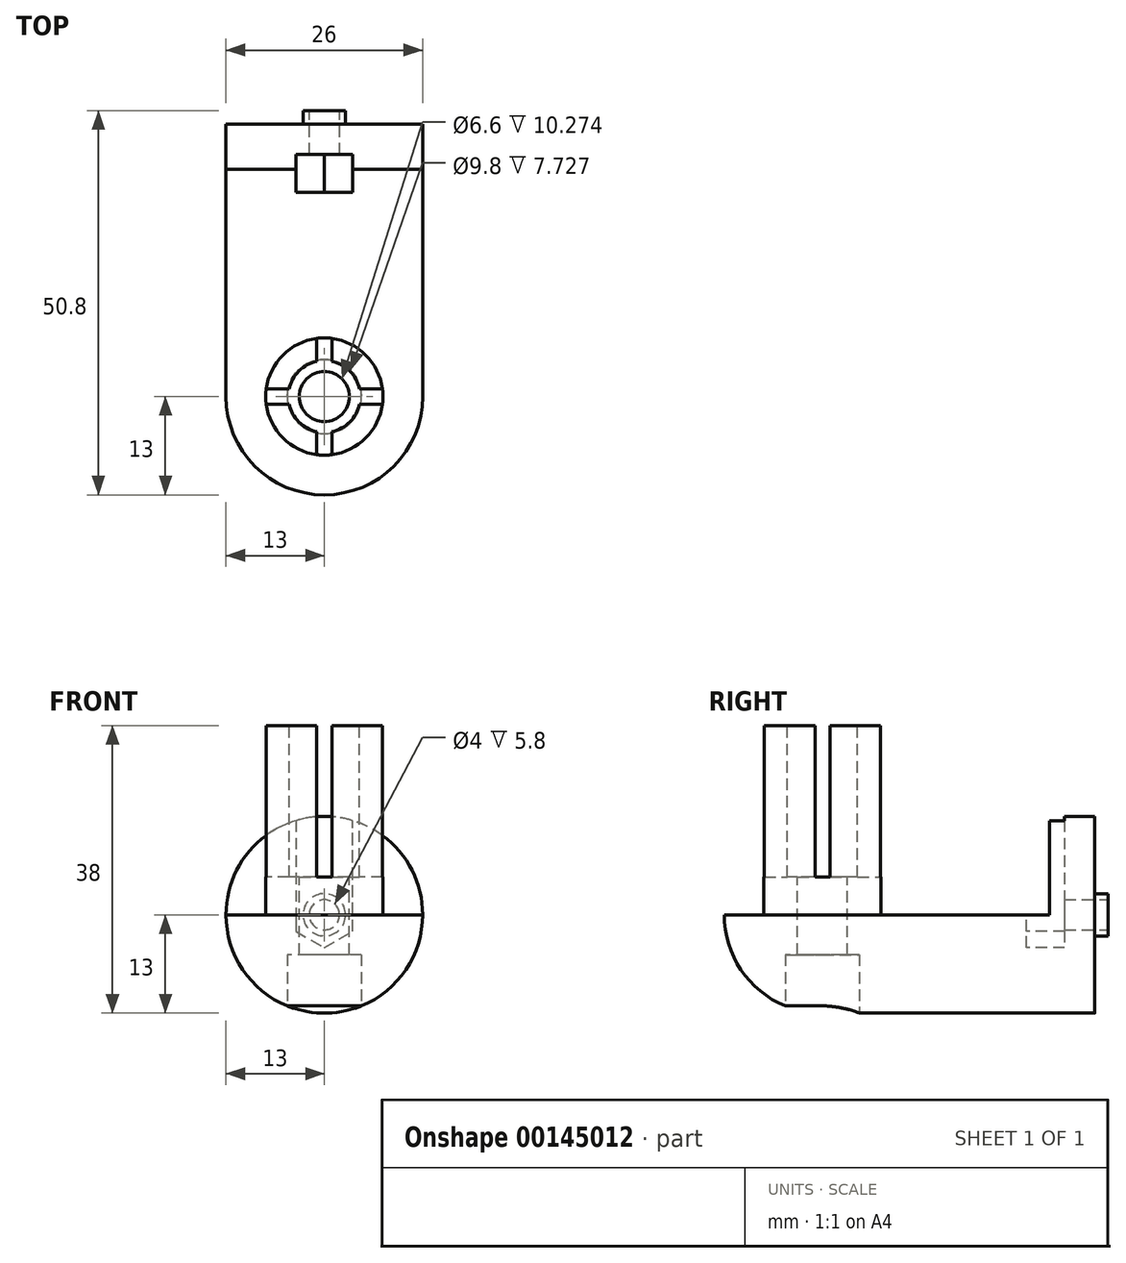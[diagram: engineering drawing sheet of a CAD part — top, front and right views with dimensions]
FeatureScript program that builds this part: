
annotation { "Feature Type Name" : "Feature", "Feature Type Description" : "" }
export const myFeature = defineFeature(function(context is Context, id is Id, definition is map)
    precondition{}
    {
        {
            var Q0;
            Q0=qCreatedBy(makeId("Top.planeOp"),FACE);
            var sketch = newSketch(context, id + "F0", { "sketchPlane" : qUnion([Q0])});
            skLineSegment(sketch, "E0", {"start": v(0, 0) * mm, "end": v(13, 0) * mm});
            skLineSegment(sketch, "E1", {"start": v(13, 0) * mm, "end": v(13, -30) * mm});
            skLineSegment(sketch, "E2", {"start": v(0, -43) * mm, "end": v(0, -43) * mm});
            skLineSegment(sketch, "E3", {"start": v(0, -43) * mm, "end": v(0, 0) * mm});
            skPoint(sketch, "E4.visualSharp", {"position": v(13, -43) * mm});
            skArc(sketch, "E4.filletArc", {"start": v(0, -43) * mm, "mid": v(9.2, -39.2) * mm, "end": v(13, -30) * mm});
            skSolve(sketch);
        }
        {
            var Q0;
            Q0 = qSketchRegion(id + "F0", true);
            var Q1;
            Q1=sQuery(id+"F0.wireOp",EDGE,"E3");
            revolve(context, id + "F1", {"entities" : qUnion([Q0]), "axis" : qUnion([Q1]), "revolveType" : RevolveType.ONE_DIRECTION, "angle" : 180 * degree});
        }
        {
            var Q0;
            Q0=makeQuery(id+"F1.opRevolve","SWEPT_FACE",FACE,{"disambiguationData":[OSD([sQuery(id+"F0.wireOp",EDGE,"E0")])]});
            var sketch = newSketch(context, id + "F2", { "sketchPlane" : qUnion([Q0])});
            skCircle(sketch, "E5", {"center": v(0, 0) * mm, "radius": 13 * mm});
            skSolve(sketch);
        }
        {
            var Q0;
            Q0 = qSketchRegion(id + "F2", true);
            extrude(context, id + "F3", {"entities" : qUnion([Q0]), "operationType" : NewBodyOperationType.ADD, "depth" : 6 * mm});
        }
        {
            var Q0;
            Q0=makeQuery(id+"F3.opExtrude","CAP_FACE",FACE,{"disambiguationData":[OSD([sQuery(id+"F2.wireOp",EDGE,"E5")])],"isStart":false});
            var sketch = newSketch(context, id + "F4", { "sketchPlane" : qUnion([Q0])});
            skCircle(sketch, "E6", {"center": v(0, 0) * mm, "radius": 2 * mm});
            skSolve(sketch);
        }
        {
            var Q0;
            Q0 = qSketchRegion(id + "F4", true);
            extrude(context, id + "F5", {"entities" : qUnion([Q0]), "operationType" : NewBodyOperationType.REMOVE, "oppositeDirection" : true, "depth" : 6 * mm});
        }
        {
            var Q0;
            Q0=makeQuery(id+"F5.boolean.opBoolean","COPY",FACE,{"derivedFrom":makeQuery(id+"F5.opExtrude","CAP_FACE",FACE,{"disambiguationData":[OSD([sQuery(id+"F4.wireOp",EDGE,"E6")])],"isStart":false})});
            var sketch = newSketch(context, id + "F6", { "sketchPlane" : qUnion([Q0])});
            skCircle(sketch, "E7.cCircle", {"center": v(0, 0) * mm, "radius": 3.75 * mm, "construction": true});
            skLineSegment(sketch, "E7.0", {"start": v(0, 4.33) * mm, "end": v(3.75, 2.17) * mm});
            skLineSegment(sketch, "E7.1", {"start": v(3.75, 2.17) * mm, "end": v(3.75, -2.17) * mm});
            skLineSegment(sketch, "E7.2", {"start": v(3.75, -2.17) * mm, "end": v(0, -4.33) * mm});
            skLineSegment(sketch, "E7.3", {"start": v(0, -4.33) * mm, "end": v(-3.75, -2.17) * mm});
            skLineSegment(sketch, "E7.4", {"start": v(-3.75, -2.17) * mm, "end": v(-3.75, 2.17) * mm});
            skLineSegment(sketch, "E7.5", {"start": v(-3.75, 2.17) * mm, "end": v(0, 4.33) * mm});
            skPoint(sketch, "E7.0.midPoint", {"position": v(1.88, 3.25) * mm});
            skSolve(sketch);
        }
        {
            var Q0;
            Q0 = qSketchRegion(id + "F6", true);
            extrude(context, id + "F7", {"entities" : qUnion([Q0]), "operationType" : NewBodyOperationType.REMOVE, "depth" : 2 * mm});
        }
        {
            var Q0;
            Q0=makeQuery(id+"F7.boolean.opBoolean","COPY",FACE,{"derivedFrom":makeQuery(id+"F7.opExtrude","CAP_FACE",FACE,{"disambiguationData":[OSD([sQuery(id+"F6.wireOp",EDGE,"E7.0"),sQuery(id+"F6.wireOp",EDGE,"E7.1"),sQuery(id+"F6.wireOp",EDGE,"E7.2"),sQuery(id+"F6.wireOp",EDGE,"E7.3"),sQuery(id+"F6.wireOp",EDGE,"E7.4"),sQuery(id+"F6.wireOp",EDGE,"E7.5")])],"isStart":false})});
            extrude(context, id + "F8", {"entities" : qUnion([Q0]), "operationType" : NewBodyOperationType.REMOVE, "depth" : 5 * mm});
        }
        {
            var Q0;
            Q0=makeQuery(id+"F7.boolean.opBoolean","MERGE",FACE,{"derivedFrom":[makeQuery(id+"F5.boolean.opBoolean","COPY",FACE,{"derivedFrom":makeQuery(id+"F5.opExtrude","CAP_FACE",FACE,{"disambiguationData":[OSD([sQuery(id+"F4.wireOp",EDGE,"E6")])],"isStart":false})}),makeQuery(id+"F7.opExtrude","CAP_FACE",FACE,{"disambiguationData":[OSD([sQuery(id+"F6.wireOp",EDGE,"E7.0"),sQuery(id+"F6.wireOp",EDGE,"E7.1"),sQuery(id+"F6.wireOp",EDGE,"E7.2"),sQuery(id+"F6.wireOp",EDGE,"E7.3"),sQuery(id+"F6.wireOp",EDGE,"E7.4"),sQuery(id+"F6.wireOp",EDGE,"E7.5")])],"isStart":true})]});
            extrude(context, id + "F9", {"entities" : qUnion([Q0]), "operationType" : NewBodyOperationType.REMOVE, "oppositeDirection" : true, "depth" : 3 * mm});
        }
        {
            var Q0;
            Q0=makeQuery(id+"F3.opExtrude","CAP_FACE",FACE,{"disambiguationData":[OSD([sQuery(id+"F2.wireOp",EDGE,"E5")])],"isStart":true});
            var sketch = newSketch(context, id + "F10", { "sketchPlane" : qUnion([Q0])});
            skLineSegment(sketch, "E8", {"start": v(3.75, 2.17) * mm, "end": v(-3.75, 2.17) * mm});
            skLineSegment(sketch, "E9", {"start": v(-3.75, 2.17) * mm, "end": v(-3.75, 14.3) * mm});
            skLineSegment(sketch, "E10", {"start": v(-3.75, 14.3) * mm, "end": v(3.75, 14.3) * mm});
            skLineSegment(sketch, "E11", {"start": v(3.75, 14.3) * mm, "end": v(3.75, 2.17) * mm});
            skSolve(sketch);
        }
        {
            var Q0;
            Q0 = qSketchRegion(id + "F10", true);
            extrude(context, id + "F11", {"entities" : qUnion([Q0]), "operationType" : NewBodyOperationType.REMOVE, "oppositeDirection" : true, "depth" : 2 * mm});
        }
        {
            var Q0;
            Q0=makeQuery(id+"F3.opExtrude","CAP_FACE",FACE,{"disambiguationData":[OSD([sQuery(id+"F2.wireOp",EDGE,"E5")])],"isStart":false});
            var sketch = newSketch(context, id + "F12", { "sketchPlane" : qUnion([Q0])});
            skCircle(sketch, "E12", {"center": v(0, 0) * mm, "radius": 2.8 * mm});
            skSolve(sketch);
        }
        {
            var Q0;
            Q0=makeQuery(id+"F12.imprint","IMPRINT",FACE,{"disambiguationData":[TD([[makeQuery(id+"F12.imprint","IMPRINT",EDGE,{"derivedFrom":sQuery(id+"F12.wireOp",EDGE,"E12")}),1.0]])]});
            extrude(context, id + "F13", {"entities" : qUnion([Q0]), "operationType" : NewBodyOperationType.ADD, "depth" : 1.8 * mm});
        }
        {
            var Q0;
            Q0=makeQuery(id+"F1.opRevolve","CAP_FACE",FACE,{"disambiguationData":[OSD([sQuery(id+"F0.wireOp",EDGE,"E0"),sQuery(id+"F0.wireOp",EDGE,"E1"),sQuery(id+"F0.wireOp",EDGE,"E3"),sQuery(id+"F0.wireOp",EDGE,"E4.filletArc")])],"isStart":false});
            var sketch = newSketch(context, id + "F14", { "sketchPlane" : qUnion([Q0])});
            skCircle(sketch, "E13", {"center": v(0, -30) * mm, "radius": 3.3 * mm});
            skSolve(sketch);
        }
        {
            var Q0;
            Q0 = qSketchRegion(id + "F14", true);
            extrude(context, id + "F15", {"entities" : qUnion([Q0]), "operationType" : NewBodyOperationType.REMOVE, "oppositeDirection" : true, "depth" : 25 * mm});
        }
        {
            var Q0;
            Q0=makeQuery(id+"F15.boolean.opBoolean","INTERSECT",EDGE,{"derivedFrom":[makeQuery(id+"F1.opRevolve","SWEPT_FACE",FACE,{"disambiguationData":[OSD([sQuery(id+"F0.wireOp",EDGE,"E4.filletArc")])]}),makeQuery(id+"F15.opExtrude","SWEPT_FACE",FACE,{"disambiguationData":[OSD([sQuery(id+"F14.wireOp",EDGE,"E13")])]})]});
            var Q1;
            Q1=makeQuery(id+"F15.boolean.opBoolean","INTERSECT",VERTEX,{"disambiguationData":[OD(1.0)],"derivedFrom":[makeQuery(id+"F1.opRevolve","SWEPT_FACE",FACE,{"disambiguationData":[OSD([sQuery(id+"F0.wireOp",EDGE,"E4.filletArc")])]}),makeQuery(id+"F3.boolean.opBoolean","MERGE",FACE,{"derivedFrom":[makeQuery(id+"F1.opRevolve","SWEPT_FACE",FACE,{"disambiguationData":[OSD([sQuery(id+"F0.wireOp",EDGE,"E1")])]}),makeQuery(id+"F3.opExtrude","SWEPT_FACE",FACE,{"disambiguationData":[OSD([sQuery(id+"F2.wireOp",EDGE,"E5")])]})]}),makeQuery(id+"F15.opExtrude","SWEPT_FACE",FACE,{"disambiguationData":[OSD([sQuery(id+"F14.wireOp",EDGE,"E13")])]})]});
            cPlane(context, id + "F16", {"entities" : qUnion([Q0, Q1]), "cplaneType" : CPlaneType.LINE_POINT, "offset" : 25 * mm, "width" : 150 * mm, "height" : 150 * mm});
        }
        {
            var Q0;
            Q0=qCreatedBy(id+"F16.planeOp",FACE);
            var sketch = newSketch(context, id + "F17", { "sketchPlane" : qUnion([Q0])});
            skCircle(sketch, "E14", {"center": v(0, -30) * mm, "radius": 4.9 * mm});
            skSolve(sketch);
        }
        {
            var Q0;
            Q0 = qSketchRegion(id + "F17", true);
            extrude(context, id + "F18", {"entities" : qUnion([Q0]), "operationType" : NewBodyOperationType.REMOVE, "depth" : 7.3 * mm});
        }
        {
            var Q0;
            Q0=makeQuery(id+"F18.boolean.opBoolean","COPY",FACE,{"derivedFrom":makeQuery(id+"F18.opExtrude","CAP_FACE",FACE,{"disambiguationData":[OSD([sQuery(id+"F17.wireOp",EDGE,"E14")])],"isStart":false})});
            extrude(context, id + "F19", {"entities" : qUnion([Q0]), "operationType" : NewBodyOperationType.REMOVE, "depth" : 25 * mm});
        }
        {
            var Q0;
            Q0=makeQuery(id+"F1.opRevolve","CAP_FACE",FACE,{"disambiguationData":[OSD([sQuery(id+"F0.wireOp",EDGE,"E0"),sQuery(id+"F0.wireOp",EDGE,"E1"),sQuery(id+"F0.wireOp",EDGE,"E3"),sQuery(id+"F0.wireOp",EDGE,"E4.filletArc")])],"isStart":false});
            var sketch = newSketch(context, id + "F20", { "sketchPlane" : qUnion([Q0])});
            skCircle(sketch, "E15", {"center": v(0, -30) * mm, "radius": 7.75 * mm});
            skSolve(sketch);
        }
        {
            var Q0;
            Q0=makeQuery(id+"F20.imprint","IMPRINT",FACE,{"disambiguationData":[TD([[makeQuery(id+"F20.imprint","IMPRINT",EDGE,{"derivedFrom":sQuery(id+"F20.wireOp",EDGE,"E15")}),1.0]])]});
            extrude(context, id + "F21", {"entities" : qUnion([Q0]), "operationType" : NewBodyOperationType.ADD, "depth" : 25 * mm});
        }
        {
            var Q0;
            Q0=makeQuery(id+"F21.opExtrude","CAP_FACE",FACE,{"disambiguationData":[OSD([sQuery(id+"F14.wireOp",EDGE,"E13"),sQuery(id+"F20.wireOp",EDGE,"E15")])],"isStart":false});
            var sketch = newSketch(context, id + "F22", { "sketchPlane" : qUnion([Q0])});
            skCircle(sketch, "E16", {"center": v(0, -30) * mm, "radius": 4.75 * mm});
            skLineSegment(sketch, "E17.bottom", {"start": v(1, -40.1) * mm, "end": v(-1, -40.1) * mm});
            skLineSegment(sketch, "E17.top", {"start": v(1, -19.9) * mm, "end": v(-1, -19.9) * mm});
            skLineSegment(sketch, "E17.left", {"start": v(1, -40.1) * mm, "end": v(1, -19.9) * mm});
            skLineSegment(sketch, "E17.right", {"start": v(-1, -40.1) * mm, "end": v(-1, -19.9) * mm});
            skLineSegment(sketch, "E18.bottom", {"start": v(10.75, -29) * mm, "end": v(-10.75, -29) * mm});
            skLineSegment(sketch, "E18.top", {"start": v(10.75, -31) * mm, "end": v(-10.75, -31) * mm});
            skLineSegment(sketch, "E18.left", {"start": v(10.75, -29) * mm, "end": v(10.75, -31) * mm});
            skLineSegment(sketch, "E18.right", {"start": v(-10.75, -29) * mm, "end": v(-10.75, -31) * mm});
            skSolve(sketch);
        }
        {
            var Q0;
            Q0 = qSketchRegion(id + "F22", true);
            extrude(context, id + "F23", {"entities" : qUnion([Q0]), "operationType" : NewBodyOperationType.REMOVE, "oppositeDirection" : true, "depth" : 20 * mm});
        }
    });
